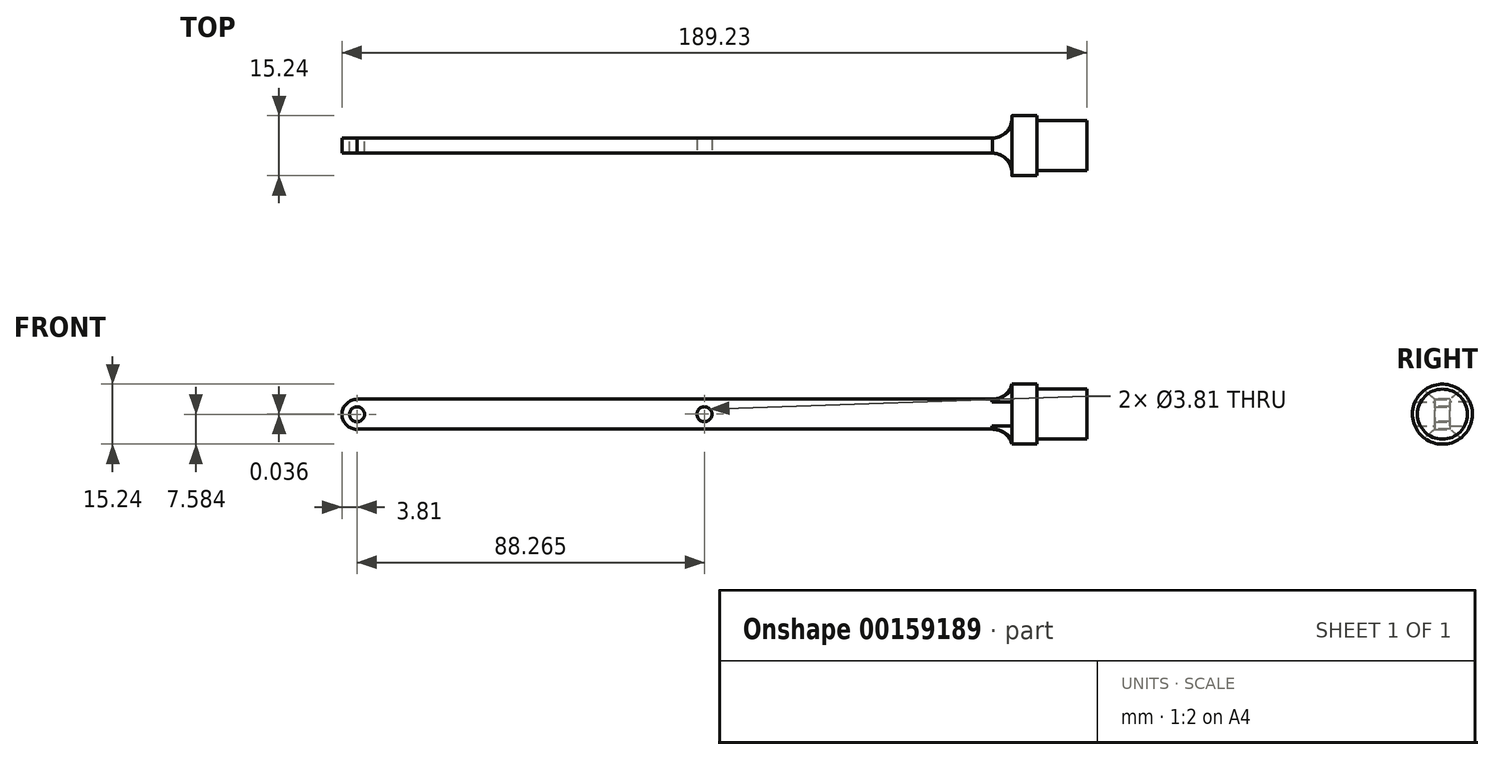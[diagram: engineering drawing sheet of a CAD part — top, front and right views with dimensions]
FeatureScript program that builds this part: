
annotation { "Feature Type Name" : "Feature", "Feature Type Description" : "" }
export const myFeature = defineFeature(function(context is Context, id is Id, definition is map)
    precondition{}
    {
        {
            var Q0;
            Q0=qCreatedBy(makeId("Right.planeOp"),FACE);
            var sketch = newSketch(context, id + "F0", { "sketchPlane" : qUnion([Q0])});
            skCircle(sketch, "E0", {"center": v(0, 0) * mm, "radius": 7.62 * mm});
            skSolve(sketch);
        }
        {
            var Q0;
            Q0=makeQuery(id+"F0.imprint","IMPRINT",FACE,{"disambiguationData":[TD([[makeQuery(id+"F0.imprint","IMPRINT",EDGE,{"derivedFrom":sQuery(id+"F0.wireOp",EDGE,"E0")}),1.0]])]});
            extrude(context, id + "F1", {"entities" : qUnion([Q0]), "depth" : 165.1 * mm});
        }
        {
            var Q0;
            Q0=makeQuery(id+"F1.opExtrude","CAP_FACE",FACE,{"disambiguationData":[OSD([sQuery(id+"F0.wireOp",EDGE,"E0")])],"isStart":false});
            var sketch = newSketch(context, id + "F2", { "sketchPlane" : qUnion([Q0])});
            skCircle(sketch, "E1", {"center": v(0, 0) * mm, "radius": 6.35 * mm});
            skSolve(sketch);
        }
        {
            var Q0;
            Q0=makeQuery(id+"F2.imprint","IMPRINT",FACE,{"disambiguationData":[TD([[makeQuery(id+"F2.imprint","IMPRINT",EDGE,{"derivedFrom":sQuery(id+"F2.wireOp",EDGE,"E1")}),1.0]])]});
            extrude(context, id + "F3", {"entities" : qUnion([Q0]), "operationType" : NewBodyOperationType.ADD, "depth" : 12.7 * mm});
        }
        {
            var Q0;
            Q0=makeQuery(id+"F1.opExtrude","CAP_FACE",FACE,{"disambiguationData":[OSD([sQuery(id+"F0.wireOp",EDGE,"E0")])],"isStart":true});
            var sketch = newSketch(context, id + "F4", { "sketchPlane" : qUnion([Q0])});
            skLineSegment(sketch, "E2.bottom", {"start": v(-1.9, 3.8) * mm, "end": v(1.9, 3.8) * mm});
            skLineSegment(sketch, "E2.top", {"start": v(-1.9, -3.81) * mm, "end": v(1.9, -3.81) * mm});
            skLineSegment(sketch, "E2.left", {"start": v(-1.9, 3.8) * mm, "end": v(-1.9, -3.81) * mm});
            skLineSegment(sketch, "E2.right", {"start": v(1.9, 3.8) * mm, "end": v(1.9, -3.81) * mm, "construction": true});
            skPoint(sketch, "E2.middle", {"position": v(0, 0) * mm});
            skLineSegment(sketch, "E3.bottom", {"start": v(-1.9, 3.8) * mm, "end": v(-5.72, 3.8) * mm});
            skLineSegment(sketch, "E3.top", {"start": v(-1.9, -3.8) * mm, "end": v(-5.71, -3.81) * mm});
            skLineSegment(sketch, "E3.left", {"start": v(-1.9, 3.8) * mm, "end": v(-1.9, -3.8) * mm});
            skLineSegment(sketch, "E3.right", {"start": v(-5.72, 3.8) * mm, "end": v(-5.71, -3.81) * mm});
            skLineSegment(sketch, "E4", {"start": v(0, 3.8) * mm, "end": v(0, 0) * mm, "construction": true});
            skLineSegment(sketch, "E5.MirrorCS", {"start": v(1.9, 3.8) * mm, "end": v(5.72, 3.8) * mm});
            skLineSegment(sketch, "E6.MirrorCS", {"start": v(1.9, 3.8) * mm, "end": v(1.9, -3.8) * mm});
            skLineSegment(sketch, "E7.MirrorCS", {"start": v(5.72, 3.8) * mm, "end": v(5.71, -3.81) * mm});
            skLineSegment(sketch, "E8.MirrorCS", {"start": v(1.9, -3.81) * mm, "end": v(5.71, -3.81) * mm});
            skSolve(sketch);
        }
        {
            var Q0;
            Q0=makeQuery(id+"F4.imprint","IMPRINT",FACE,{"disambiguationData":[TD([[makeQuery(id+"F4.imprint","IMPRINT",EDGE,{"derivedFrom":sQuery(id+"F4.wireOp",EDGE,"E2.bottom")}),-1.0]])]});
            extrude(context, id + "F5", {"entities" : qUnion([Q0]), "operationType" : NewBodyOperationType.ADD, "depth" : 7.62 * mm});
        }
        {
            var Q0;
            Q0=qCreatedBy(makeId("Front.planeOp"),FACE);
            var sketch = newSketch(context, id + "F6", { "sketchPlane" : qUnion([Q0])});
            skLineSegment(sketch, "E9", {"start": v(-7.62, 3.77) * mm, "end": v(-7.62, 1.87) * mm});
            skArc(sketch, "E10", {"start": v(-7.62, 3.77) * mm, "mid": v(-11.43, -0.04) * mm, "end": v(-7.62, -3.85) * mm});
            skCircle(sketch, "E11", {"center": v(-7.62, -0.04) * mm, "radius": 1.9 * mm});
            skLineSegment(sketch, "E12.trimOffspring", {"start": v(-7.62, -1.94) * mm, "end": v(-7.62, -3.85) * mm});
            skSolve(sketch);
        }
        {
            var Q0;
            {var subQ0=sQuery(id+"F6.wireOp",EDGE,"E9");Q0=makeQuery(id+"F6.imprint","IMPRINT",FACE,{"disambiguationData":[TD([[makeQuery(id+"F6.imprint","IMPRINT",EDGE,{"derivedFrom":subQ0}),-1.0]])]});}
            extrude(context, id + "F7", {"entities" : qUnion([Q0]), "operationType" : NewBodyOperationType.ADD, "endBound" : BoundingType.SYMMETRIC, "depth" : 3.8 * mm});
        }
        {
            var Q0;
            {var subQ0=sQuery(id+"F6.wireOp",EDGE,"E11");var subQ1=makeQuery(id+"F6.imprint","INTERSECT",VERTEX,{"derivedFrom":[sQuery(id+"F6.wireOp",EDGE,"E9"),subQ0]});Q0=makeQuery(id+"F6.imprint","IMPRINT",FACE,{"disambiguationData":[TD([[makeQuery(id+"F6.imprint","IMPRINT",EDGE,{"disambiguationData":[TD([[subQ1,-1.0]])],"derivedFrom":subQ0}),1.0]])]});}
            extrude(context, id + "F8", {"entities" : qUnion([Q0]), "operationType" : NewBodyOperationType.REMOVE, "endBound" : BoundingType.THROUGH_ALL, "oppositeDirection" : true, "depth" : 25.4 * mm});
        }
        {
            var Q0;
            {var subQ0=sQuery(id+"F6.wireOp",EDGE,"E11");var subQ1=makeQuery(id+"F6.imprint","INTERSECT",VERTEX,{"derivedFrom":[sQuery(id+"F6.wireOp",EDGE,"E9"),subQ0]});Q0=makeQuery(id+"F6.imprint","IMPRINT",FACE,{"disambiguationData":[TD([[makeQuery(id+"F6.imprint","IMPRINT",EDGE,{"disambiguationData":[TD([[subQ1,-1.0]])],"derivedFrom":subQ0}),1.0]])]});}
            extrude(context, id + "F9", {"entities" : qUnion([Q0]), "operationType" : NewBodyOperationType.REMOVE, "depth" : 25.4 * mm});
        }
        {
            var Q0;
            Q0=qCreatedBy(makeId("Top.planeOp"),FACE);
            var sketch = newSketch(context, id + "F10", { "sketchPlane" : qUnion([Q0])});
            skLineSegment(sketch, "E13.bottom", {"start": v(0, 7.62) * mm, "end": v(158.75, 7.62) * mm});
            skLineSegment(sketch, "E13.top", {"start": v(0, 1.9) * mm, "end": v(158.75, 1.9) * mm});
            skLineSegment(sketch, "E13.left", {"start": v(0, 7.62) * mm, "end": v(0, 1.9) * mm});
            skLineSegment(sketch, "E13.right", {"start": v(158.75, 7.62) * mm, "end": v(158.75, 1.9) * mm});
            skLineSegment(sketch, "E14", {"start": v(0, 0) * mm, "end": v(5.29, 0) * mm, "construction": true});
            skLineSegment(sketch, "E15.MirrorCS", {"start": v(158.75, -7.62) * mm, "end": v(158.75, -1.9) * mm});
            skLineSegment(sketch, "E16.MirrorCS", {"start": v(0, -7.62) * mm, "end": v(158.75, -7.62) * mm});
            skLineSegment(sketch, "E17.MirrorCS", {"start": v(0, -1.9) * mm, "end": v(158.75, -1.9) * mm});
            skLineSegment(sketch, "E18.MirrorCS", {"start": v(0, -7.62) * mm, "end": v(0, -1.9) * mm});
            skSolve(sketch);
        }
        {
            var Q0;
            Q0=qSketchRegion(id+"F10",true);
            extrude(context, id + "F11", {"entities" : qUnion([Q0]), "operationType" : NewBodyOperationType.REMOVE, "endBound" : BoundingType.THROUGH_ALL, "oppositeDirection" : true, "depth" : 25.4 * mm, "hasSecondDirection" : true, "secondDirectionOppositeDirection" : false, "secondDirectionDepth" : 25.4 * mm});
        }
        {
            var Q0;
            Q0=makeQuery(id+"F11.boolean.opBoolean","MERGE",FACE,{"derivedFrom":[makeQuery(id+"F7.boolean.opBoolean","MERGE",FACE,{"derivedFrom":[makeQuery(id+"F5.opExtrude","SWEPT_FACE",FACE,{"disambiguationData":[OSD([sQuery(id+"F4.wireOp",EDGE,"E6.MirrorCS")])]}),makeQuery(id+"F7.opExtrude","CAP_FACE",FACE,{"disambiguationData":[OSD([sQuery(id+"F6.wireOp",EDGE,"E9"),sQuery(id+"F6.wireOp",EDGE,"E10"),sQuery(id+"F6.wireOp",EDGE,"E11"),sQuery(id+"F6.wireOp",EDGE,"E12.trimOffspring")])],"isStart":false})]}),makeQuery(id+"F11.opExtrude","SWEPT_FACE",FACE,{"disambiguationData":[OSD([sQuery(id+"F10.wireOp",EDGE,"E17.MirrorCS")])]})]});
            var sketch = newSketch(context, id + "F12", { "sketchPlane" : qUnion([Q0])});
            skCircle(sketch, "E19", {"center": v(80.65, 0) * mm, "radius": 1.9 * mm});
            skLineSegment(sketch, "E20.bottom", {"start": v(0, 3.81) * mm, "end": v(158.75, 3.81) * mm});
            skLineSegment(sketch, "E20.left", {"start": v(0, 3.81) * mm, "end": v(0, 7.38) * mm});
            skLineSegment(sketch, "E20.right", {"start": v(158.75, 3.81) * mm, "end": v(158.75, 7.38) * mm});
            skLineSegment(sketch, "E21.bottom", {"start": v(0, -3.81) * mm, "end": v(158.75, -3.81) * mm});
            skLineSegment(sketch, "E21.left", {"start": v(0, -3.81) * mm, "end": v(0, -7.38) * mm});
            skLineSegment(sketch, "E21.right", {"start": v(158.75, -3.81) * mm, "end": v(158.75, -7.38) * mm});
            skPoint(sketch, "E22.oppositeSnap0", {"position": v(0, 5.6) * mm});
            skLineSegment(sketch, "E22.top", {"start": v(158.75, 10.08) * mm, "end": v(0, 10.08) * mm});
            skLineSegment(sketch, "E22.left", {"start": v(158.75, 7.38) * mm, "end": v(158.75, 10.08) * mm});
            skLineSegment(sketch, "E22.right", {"start": v(0, 7.38) * mm, "end": v(0, 10.08) * mm});
            skLineSegment(sketch, "E23.top", {"start": v(0, -11.5) * mm, "end": v(158.75, -11.5) * mm});
            skLineSegment(sketch, "E23.left", {"start": v(0, -7.38) * mm, "end": v(0, -11.5) * mm});
            skLineSegment(sketch, "E23.right", {"start": v(158.75, -7.38) * mm, "end": v(158.75, -11.5) * mm});
            skSolve(sketch);
        }
        {
            var Q0;
            Q0 = qSketchRegion(id + "F12", true);
            extrude(context, id + "F13", {"entities" : qUnion([Q0]), "operationType" : NewBodyOperationType.REMOVE, "endBound" : BoundingType.THROUGH_ALL, "oppositeDirection" : true, "depth" : 25.4 * mm});
        }
        {
            var Q0;
            Q0=makeQuery(id+"F11.boolean.opBoolean","COPY",EDGE,{"derivedFrom":makeQuery(id+"F11.opExtrude","SWEPT_EDGE",EDGE,{"disambiguationData":[OSD([sQuery(id+"F10.wireOp",EDGE,"E15.MirrorCS"),sQuery(id+"F10.wireOp",EDGE,"E17.MirrorCS")])]})});
            var Q1;
            Q1=makeQuery(id+"F13.boolean.opBoolean","COPY",EDGE,{"derivedFrom":makeQuery(id+"F13.opExtrude","SWEPT_EDGE",EDGE,{"disambiguationData":[OSD([sQuery(id+"F10.wireOp",EDGE,"E15.MirrorCS"),sQuery(id+"F10.wireOp",EDGE,"E17.MirrorCS"),sQuery(id+"F12.wireOp",EDGE,"E20.bottom"),sQuery(id+"F12.wireOp",EDGE,"E20.right")])]})});
            var Q2;
            Q2=makeQuery(id+"F13.boolean.opBoolean","COPY",EDGE,{"derivedFrom":makeQuery(id+"F13.opExtrude","SWEPT_EDGE",EDGE,{"disambiguationData":[OSD([sQuery(id+"F10.wireOp",EDGE,"E15.MirrorCS"),sQuery(id+"F10.wireOp",EDGE,"E17.MirrorCS"),sQuery(id+"F12.wireOp",EDGE,"E21.bottom"),sQuery(id+"F12.wireOp",EDGE,"E21.right")])]})});
            var Q3;
            Q3=makeQuery(id+"F11.boolean.opBoolean","COPY",EDGE,{"derivedFrom":makeQuery(id+"F11.opExtrude","SWEPT_EDGE",EDGE,{"disambiguationData":[OSD([sQuery(id+"F10.wireOp",EDGE,"E13.top"),sQuery(id+"F10.wireOp",EDGE,"E13.right")])]})});
            fillet(context, id + "F14", {"entities" : qUnion([Q0, Q1, Q2, Q3]), "radius" : 5.08 * mm, "tangentPropagation" : true, "allowEdgeOverflow" : false});
        }
    });
